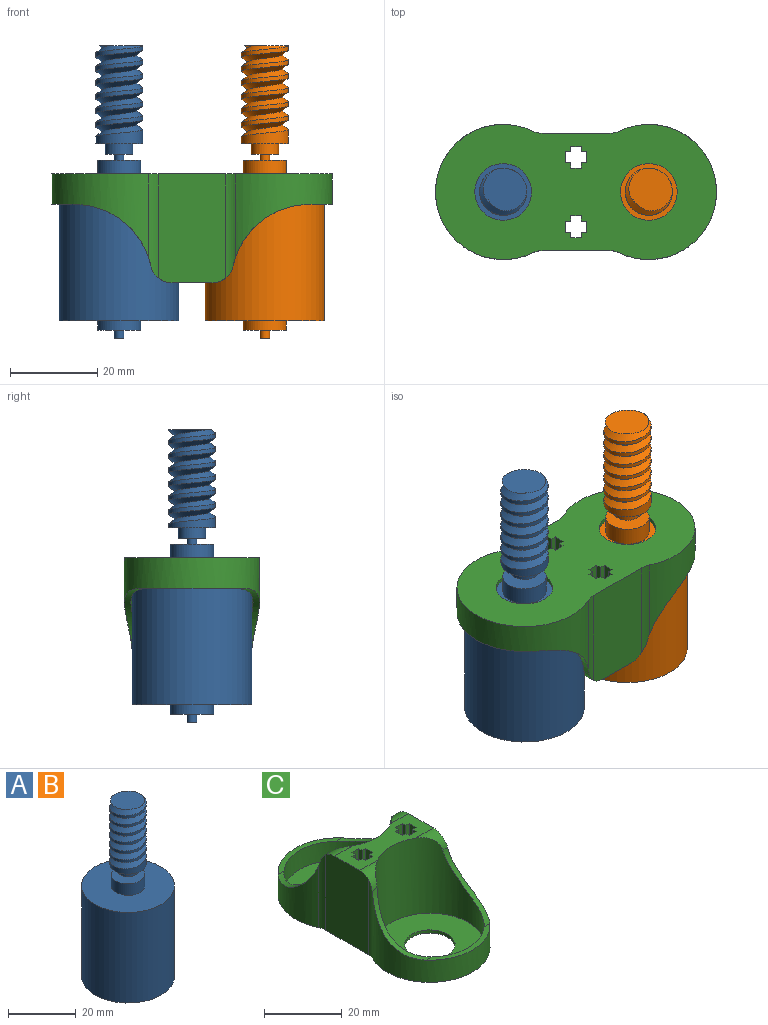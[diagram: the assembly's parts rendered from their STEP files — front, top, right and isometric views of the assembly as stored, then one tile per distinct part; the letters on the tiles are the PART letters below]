
ASSEMBLY  parts=3 mates=2
PART A: 18 faces, bbox 28.3x28.3x69 mm
  f0: cylinder r=5.4mm len=22.4mm, axis (0,0,-1), area 253.8mm2, adj f13,f14,f15,f16,f17
  f1: plane 2.2x2.2mm, normal (0,0,-1), area 3.8mm2, adj f2
  f2: cylinder r=1.1mm len=2.2mm, axis (0,0,-1), area 12.5mm2, adj f1,f3
  f3: plane 9.93x9.93mm, normal (0,0,-1), area 73.6mm2, adj f2,f4
  f4: cylinder r=4.96mm len=9.93mm, axis (0,0,-1), area 67.1mm2, adj f3,f5
  f5: plane 27.41x27.41mm, normal (0,0,-1), area 512.6mm2, adj f4,f6
  f6: cylinder r=13.71mm len=32.69mm, axis (0,0,-1), area 2815mm2, adj f5,f7
  f7: plane 27.41x27.41mm, normal (0,0,1), area 512.6mm2, adj f6,f8
  f8: cylinder r=4.96mm len=9.93mm, axis (0,0,-1), area 129.5mm2, adj f7,f9
  f9: plane 9.93x9.93mm, normal (0,0,1), area 73.6mm2, adj f8,f10
  f10: cylinder r=1.1mm len=2.2mm, axis (0,0,-1), area 9mm2, adj f9,f11
  f11: plane 6.3x6.3mm, normal (0,0,-1), area 27.4mm2, adj f10,f12
  f12: cylinder r=3.15mm len=6.3mm, axis (0,0,-1), area 49.5mm2, adj f11,f13
  f13: plane 10.8x10.8mm, normal (0,0,-1), area 60.4mm2, adj f0,f12
  f14: plane 10.84x10.65mm, normal (0,0,1), area 75.4mm2, adj f0,f15,f16
  f15: bspline ~22.46x12.47mm, area 354.6mm2, adj f0,f14,f16,f17
  f16: bspline ~23.53x12.47mm, area 371.3mm2, adj f0,f14,f15,f17
  f17: plane 2.25x1.5mm, normal (0,1,0), area 1.7mm2, adj f0,f15,f16
PART B: same geometry as A
PART C: 50 faces, bbox 31x64.4x25 mm
  f0: cylinder r=15.5mm len=31mm, axis (0,0,-1), area 555.7mm2, adj f34,f36,f37,f38,f46,f48
  f1: cylinder r=14mm len=28mm, axis (0,0,-1), area 1165.9mm2, adj f2,f4,f36,f37,f38,f47,f49
  f2: plane 26.9x9.1mm, normal (0,0,1), area 172.5mm2, adj f1,f5,f6,f7,f8,f9,f10,f11
  f3: plane 28x28mm, normal (0,0,1), area 483mm2, adj f32,f35
  f4: plane 28x28mm, normal (0,0,1), area 483mm2, adj f1,f31
  f5: plane 25x2.5mm, normal (1,0,0), area 62.5mm2, adj f2,f6,f33,f34
  f6: plane 25x1.25mm, normal (0,-1,0), area 31.2mm2, adj f2,f5,f7,f34
  f7: plane 25x1.25mm, normal (1,0,0), area 31.2mm2, adj f2,f6,f8,f34
  f8: plane 25x2.5mm, normal (0,-1,0), area 62.5mm2, adj f2,f7,f9,f34
  f9: plane 25x1.25mm, normal (-1,0,0), area 31.2mm2, adj f2,f8,f10,f34
  f10: plane 25x1.25mm, normal (0,-1,0), area 31.2mm2, adj f2,f9,f11,f34
  f11: plane 25x2.5mm, normal (-1,0,0), area 62.5mm2, adj f2,f10,f12,f34
  f12: plane 25x1.25mm, normal (0,1,0), area 31.2mm2, adj f2,f11,f13,f34
  f13: plane 25x1.25mm, normal (-1,0,0), area 31.2mm2, adj f2,f12,f14,f34
  f14: plane 25x2.5mm, normal (0,1,0), area 62.5mm2, adj f2,f13,f15,f34
  f15: plane 25x1.25mm, normal (1,0,0), area 31.2mm2, adj f2,f14,f33,f34
  f16: plane 25x1.25mm, normal (0,1,0), area 31.2mm2, adj f2,f17,f30,f34
  f17: plane 25x1.25mm, normal (-1,0,0), area 31.2mm2, adj f2,f16,f18,f34
  f18: plane 25x2.5mm, normal (0,1,0), area 62.5mm2, adj f2,f17,f19,f34
  f19: plane 25x1.25mm, normal (1,0,0), area 31.2mm2, adj f2,f18,f20,f34
  f20: plane 25x1.25mm, normal (0,1,0), area 31.2mm2, adj f2,f19,f21,f34
  f21: plane 25x2.5mm, normal (1,0,0), area 62.5mm2, adj f2,f20,f22,f34
  f22: plane 25x1.25mm, normal (0,-1,0), area 31.2mm2, adj f2,f21,f23,f34
  f23: plane 25x1.25mm, normal (1,0,0), area 31.2mm2, adj f2,f22,f24,f34
  f24: plane 25x2.5mm, normal (0,-1,0), area 62.5mm2, adj f2,f23,f25,f34
  f25: plane 25x1.25mm, normal (-1,0,0), area 31.2mm2, adj f2,f24,f26,f34
  f26: plane 25x1.25mm, normal (0,-1,0), area 31.2mm2, adj f2,f25,f30,f34
  f27: plane 25x15.54mm, normal (1,0,0), area 386mm2, adj f2,f34,f44,f45,f48,f49
  f28: cylinder r=15.5mm len=31mm, axis (0,0,-1), area 555.7mm2, adj f34,f39,f40,f41,f42,f44
  f29: plane 25x15.54mm, normal (-1,0,0), area 386mm2, adj f2,f34,f42,f43,f46,f47
  f30: plane 25x2.5mm, normal (-1,0,0), area 62.5mm2, adj f2,f16,f26,f34
  f31: cylinder r=6.5mm len=13mm, axis (0,0,-1), area 40.8mm2, adj f4,f34
  f32: cylinder r=6.5mm len=13mm, axis (0,0,-1), area 40.8mm2, adj f3,f34
  f33: plane 25x1.25mm, normal (0,1,0), area 31.2mm2, adj f2,f5,f15,f34
  f34: plane 64.4x31mm, normal (0,0,-1), area 1393.5mm2, adj f0,f5,f6,f7,f8,f9,f10,f11
  f35: cylinder r=14mm len=28mm, axis (0,0,-1), area 1165.9mm2, adj f2,f3,f39,f40,f41,f43,f45
  f36: plane 23.17x5.2mm, normal (0,0,1), area 35.3mm2, adj f0,f1,f37,f38
  f37: cylinder r=18mm len=17.57mm, axis (1,0,0), area 39.5mm2, adj f0,f1,f36,f46,f47
  f38: cylinder r=18mm len=17.57mm, axis (1,0,0), area 39.5mm2, adj f0,f1,f36,f48,f49
  f39: plane 23.17x5.2mm, normal (0,0,1), area 35.3mm2, adj f28,f35,f40,f41
  f40: cylinder r=18mm len=17.57mm, axis (1,0,0), area 39.5mm2, adj f28,f35,f39,f42,f43
  f41: cylinder r=18mm len=17.57mm, axis (1,0,0), area 39.5mm2, adj f28,f35,f39,f44,f45
  f42: cylinder r=5mm len=23.83mm, axis (0,0,-1), area 49.9mm2, adj f28,f29,f34,f40,f43
  f43: cylinder r=5mm len=6.78mm, axis (1,0,0), area 21.7mm2, adj f2,f29,f35,f40,f42
  f44: cylinder r=5mm len=23.83mm, axis (0,0,-1), area 49.9mm2, adj f27,f28,f34,f41,f45
  f45: cylinder r=5mm len=6.78mm, axis (1,0,0), area 21.7mm2, adj f2,f27,f35,f41,f44
  f46: cylinder r=5mm len=23.83mm, axis (0,0,-1), area 49.9mm2, adj f0,f29,f34,f37,f47
  f47: cylinder r=5mm len=6.78mm, axis (1,0,0), area 21.7mm2, adj f1,f2,f29,f37,f46
  f48: cylinder r=5mm len=23.83mm, axis (0,0,-1), area 49.9mm2, adj f0,f27,f34,f38,f49
  f49: cylinder r=5mm len=6.78mm, axis (1,0,0), area 21.7mm2, adj f1,f2,f27,f38,f48
PLACE A t=(-51.11,11.46,-1.6)mm
PLACE B t=(-17.71,11.46,-1.6)mm fixed
PLACE C rot(axis=(0.71,0.71,0),180deg) t=(-17.71,11.46,36.05)mm
MATE fastened B.f0 <-> A.f14  axis (0,0,1) through (-17.71,11.46,65.4)mm
MATE fastened A.f0 <-> C.f31  axis (0,0,1) through (-51.11,11.46,35.05)mm
